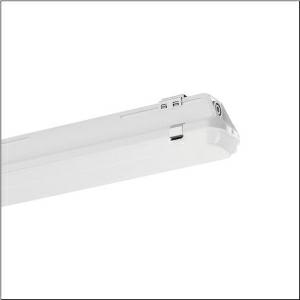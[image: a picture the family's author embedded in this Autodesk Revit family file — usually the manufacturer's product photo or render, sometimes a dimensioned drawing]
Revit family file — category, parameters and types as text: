
# Revit family: monsun_11_51fp10ep460l007
name_source: partatom
category: Lighting Fixtures
units: mm (PartAtom-declared; Revit-internal decimal feet)

## family parameters
Cut with Voids When Loaded = No
Host = Face
Light Source = No
Part Type = Normal
Room Calculation Point = No
Round Connector Dimension = Use Diameter
Shared = No

## types (1)
- --- (1 x LED, 6050 lm, 31.5 W, 4000K)
    Apparent Load = 32 VA
    CIE Flux Codes = 47 77 93 94 100
    Color Rendering = 80
    Color Temperature = 4000K
    Default Elevation = 1800 mm
    Description = Monsun 11, damp-proof luminaire, chain hanger, primary optical cover: enclosure, of PMMA, light emission: direct distribution, primary light characteristic: symmetric, installation type: suspended mounting, surface-mounted, horizontal mounting, vertical mounting, LED, rated luminous flux: 6.050lm, luminous efficacy: 192lm/W, light colour: 840, colour temperature: 4000K, control gear: DALI 2, with terminal, 5-pole, max. 2.5mm², through-wiring: 7x 2.5mm², mains connection: 220..240V, AC, 50/60Hz, rated input power: 32W, housing, of glass-fibre reinforced polyester, uncoated, bright grey, incl. chain hanger, length: 1.590mm, width: 90mm, height: 88mm, clip for enclosure, of stainless steel (V2A), ceiling mounting element, of stainless steel (V2A), chain hanger, of stainless steel (V2A), protection rating (complete): IP66, insulation class (complete): insulation class I (protective earthing), certification: CE, ENEC, VDE, UKCA, protection symbol: D, impact resistance: IK04, permissible operating ambient temperature: -25..+30°C, standard: EN 50419, EN 60598-2-1, corresponds to IFS (International Featured Standards) requirements for safety and quality in the food industry, for indoor or canopied outdoor use, no direct snow, no direct sun, no direct rain, LABS conformity tested according to VDMA 24364:2018-05, contact your sales advisor before using the luminaires in applications with unclear chemical exposure, large temperature fluctuations or condensation-forming humidity, packaging unit: 1 piece
    Height = 89 mm
    Lamp = 1 x LED
    Lamp Light Flux = 6050 lm
    Lamp Power = 31.5 W
    Lamp count = 1
    Length = 1590 mm
    Luminous efficacy = 192 lm/W
    Manufacturer = Siteco
    ModVariant = No
    Model = 51FP10EP460L007
    Mounting Place = Ceiling
    Mounting Type = Surface mounted
    Number of Poles = 1
    OnlyDefault = Yes
    Power Factor = 1
    Product Name = Monsun 11
    Product group = damp-proof luminaire
    ProductGroupID = 300
    Protection Class = Protection class I
    Protection Degree = IP 66
    RLX_Detail_Level = 1
    RLX_Emergency_Light_Flux = 0 lm
    RLX_Emergency_Type = 0
    RLX_Emergency_Type_DB = No
    RlxData = <blob elided: 92269 chars, md5=1a2d60b1>
    Socket = socket
    Standby Power = 0 W
    System Light Flux = 6050 lm
    System Power = 32 W
    Type Comments = factory setting: luminous flux: 100 % | dim-lin: 254 | 219 mA
    Type Image = l_1349237.jpg
    URL = http://relux.com
    VarID = @adj_033685
    Voltage = 0 V
    Weight = 0.00 kg
    Width = 90 mm

## geometry (parser evidence)
native form markers: Blend x4, Sweep x15
no freeform markers — native parametric forms only
